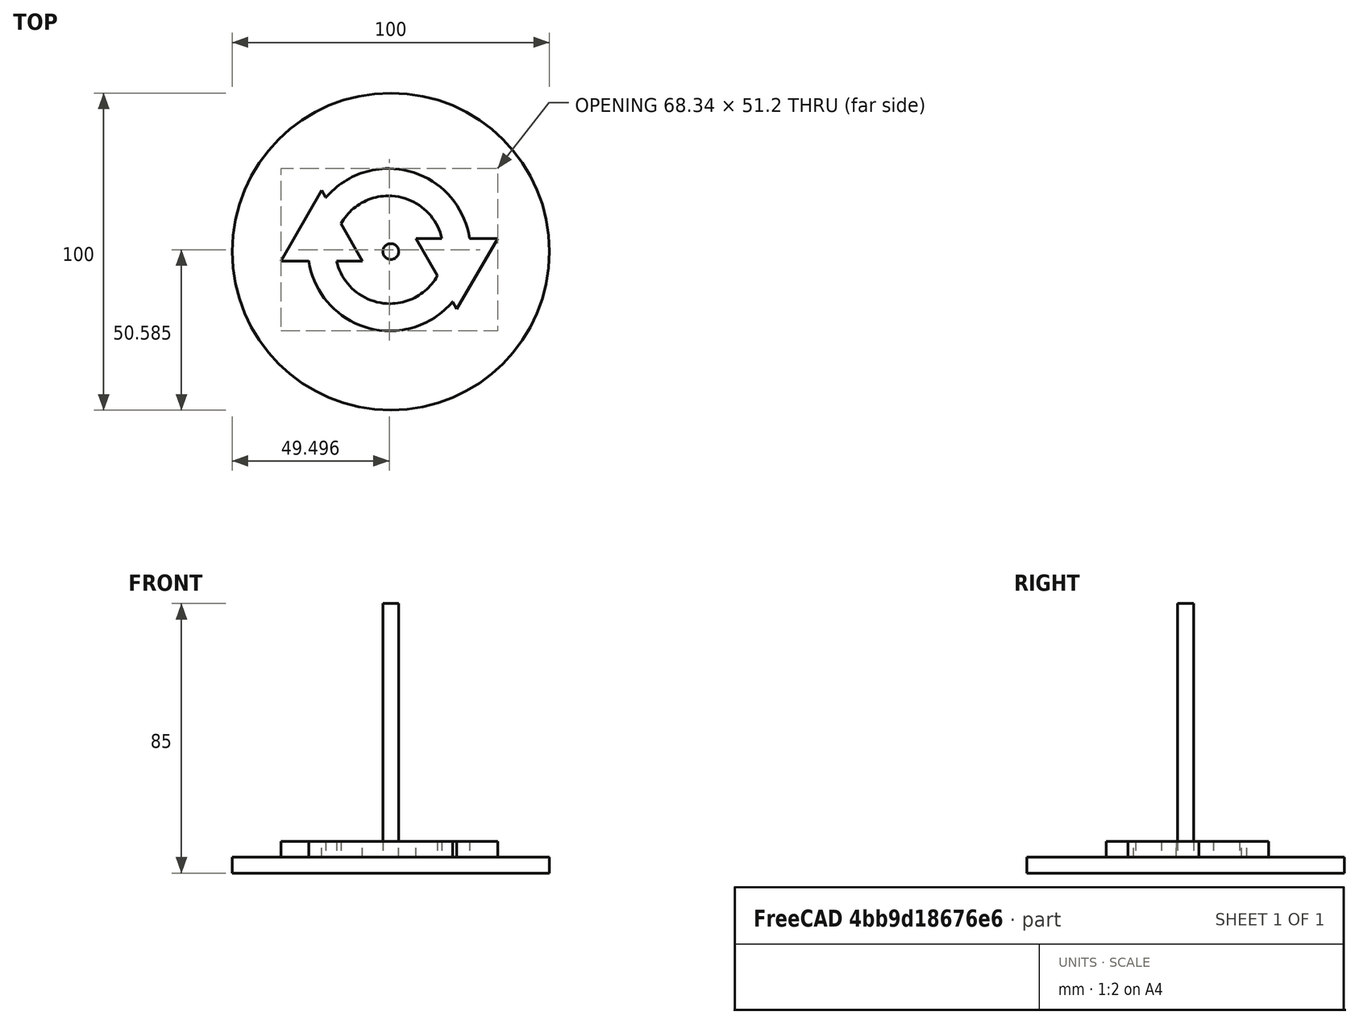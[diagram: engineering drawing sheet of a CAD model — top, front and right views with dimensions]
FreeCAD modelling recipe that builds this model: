
FCSTD DOCUMENT  (FreeCAD 0.15R4671 (Git))
Label: rotating_charge
License: All rights reserved
LicenseURL: http://en.wikipedia.org/wiki/All_rights_reserved
objects: Part::Feature×5, Part::Extrusion×4, Part::MultiFuse×1, Mesh::Feature×1
note: 10 computed .brp shape members not serialized (recipe doc carries the construction recipe); baked Part::Feature solids carry a one-line shape summary decoded from their .brp

FEATURE [Part::Feature] Shape0_301917677128
  shape: bbox 100 x 100 x 85 mm, 5 faces (baked)
FEATURE [Part::Feature] Face
  Placement = pos=(-42,37,0) rot=(0,0,1;0rad)
  shape: bbox 25.74 x 22.29 x 2e-07 mm, 1 faces, 0 solids (baked)
FEATURE [Part::Feature] Face001
  Placement = pos=(-42,37,0) rot=(0,0,1;0rad)
  shape: bbox 51.63 x 25.82 x 2e-07 mm, 1 faces, 0 solids (baked)
FEATURE [Part::Feature] Face002
  Placement = pos=(-42,37,0) rot=(0,0,1;0rad)
  shape: bbox 25.74 x 22.29 x 2e-07 mm, 1 faces, 0 solids (baked)
FEATURE [Part::Feature] Face003
  Placement = pos=(-42,37,0) rot=(0,0,1;0rad)
  shape: bbox 51.63 x 25.82 x 2e-07 mm, 1 faces, 0 solids (baked)
FEATURE [Part::Extrusion] Extrude
  Base = -> Face
  Dir = (0,0,10)
  Solid = false
FEATURE [Part::Extrusion] Extrude001
  Base = -> Face001
  Dir = (0,0,10)
  Solid = false
FEATURE [Part::Extrusion] Extrude002
  Base = -> Face002
  Dir = (0,0,10)
  Solid = false
FEATURE [Part::Extrusion] Extrude003
  Base = -> Face003
  Dir = (0,0,10)
  Solid = false
FEATURE [Part::MultiFuse] Fusion
  Shapes = -> [Shape0_301917677128,Extrude001,Extrude,Extrude002,Extrude003]
FEATURE [Mesh::Feature] Mesh  label="Fusion (Meshed)"
